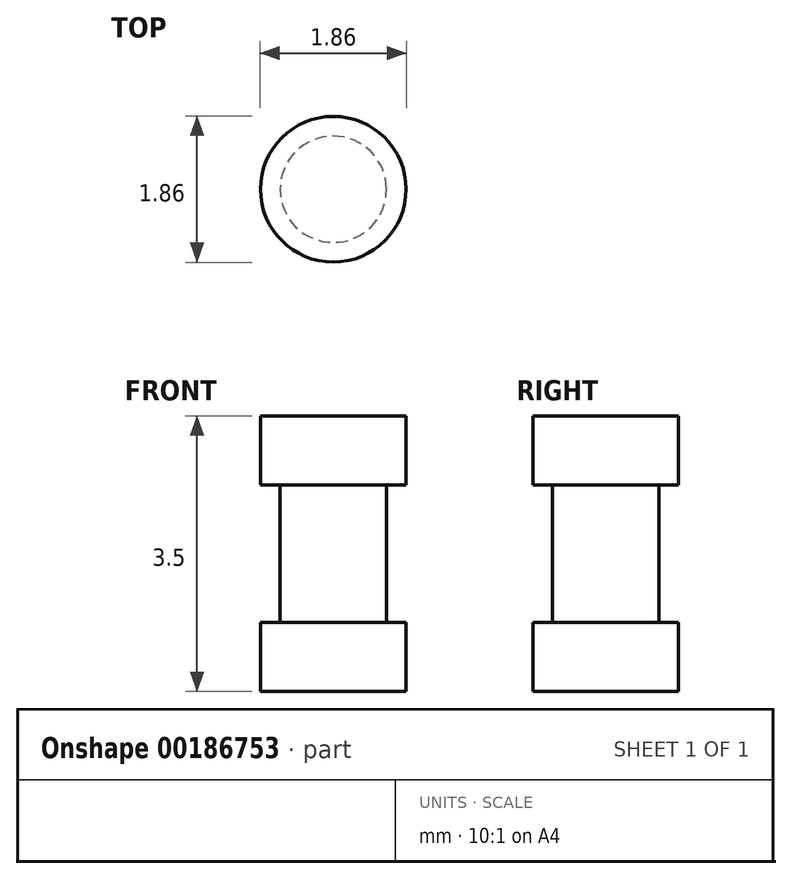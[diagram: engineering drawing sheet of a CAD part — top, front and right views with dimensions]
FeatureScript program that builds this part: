
annotation { "Feature Type Name" : "Feature", "Feature Type Description" : "" }
export const myFeature = defineFeature(function(context is Context, id is Id, definition is map)
    precondition{}
    {
        {
            var Q0;
            Q0=qCreatedBy(makeId("Front.planeOp"),FACE);
            var sketch = newSketch(context, id + "F0", { "sketchPlane" : qUnion([Q0])});
            skLineSegment(sketch, "E0", {"start": v(0, 1.75) * mm, "end": v(0.92, 1.75) * mm});
            skLineSegment(sketch, "E1", {"start": v(0.93, -1.75) * mm, "end": v(0, -1.75) * mm});
            skLineSegment(sketch, "E2", {"start": v(0, 1.75) * mm, "end": v(0, 0) * mm});
            skLineSegment(sketch, "E3", {"start": v(0, 0) * mm, "end": v(0, -1.75) * mm});
            skPoint(sketch, "E4.startSnap0", {"position": v(0.46, 1.75) * mm});
            skPoint(sketch, "E5.oppositeSnap0", {"position": v(0, 0.87) * mm});
            skLineSegment(sketch, "E5.bottom", {"start": v(0, 1.75) * mm, "end": v(0.93, 1.75) * mm});
            skLineSegment(sketch, "E5.top", {"start": v(0.68, 0.87) * mm, "end": v(0.93, 0.87) * mm});
            skLineSegment(sketch, "E5.left", {"start": v(0, 1.75) * mm, "end": v(0, 0.87) * mm});
            skLineSegment(sketch, "E5.right", {"start": v(0.93, 1.75) * mm, "end": v(0.93, 0.87) * mm});
            skPoint(sketch, "E6.oppositeSnap0", {"position": v(0, -0.88) * mm});
            skLineSegment(sketch, "E6.bottom", {"start": v(0, -1.75) * mm, "end": v(0.93, -1.75) * mm});
            skLineSegment(sketch, "E6.top", {"start": v(0.68, -0.88) * mm, "end": v(0.93, -0.88) * mm});
            skLineSegment(sketch, "E6.left", {"start": v(0, -1.75) * mm, "end": v(0, -0.88) * mm});
            skLineSegment(sketch, "E6.right", {"start": v(0.93, -1.75) * mm, "end": v(0.93, -0.88) * mm});
            skLineSegment(sketch, "E7", {"start": v(0.68, 0.87) * mm, "end": v(0.68, -0.88) * mm});
            skSolve(sketch);
        }
        {
            var Q0;
            Q0=makeQuery(id+"F0.imprint","IMPRINT",FACE,{"disambiguationData":[TD([[makeQuery(id+"F0.imprint","IMPRINT",EDGE,{"derivedFrom":sQuery(id+"F0.wireOp",EDGE,"E2")}),1.0]])]});
            var Q1;
            Q1=sQuery(id+"F0.wireOp",EDGE,"E2");
            revolve(context, id + "F1", {"entities" : qUnion([Q0]), "axis" : qUnion([Q1]), "revolveType" : RevolveType.FULL});
        }
    });
